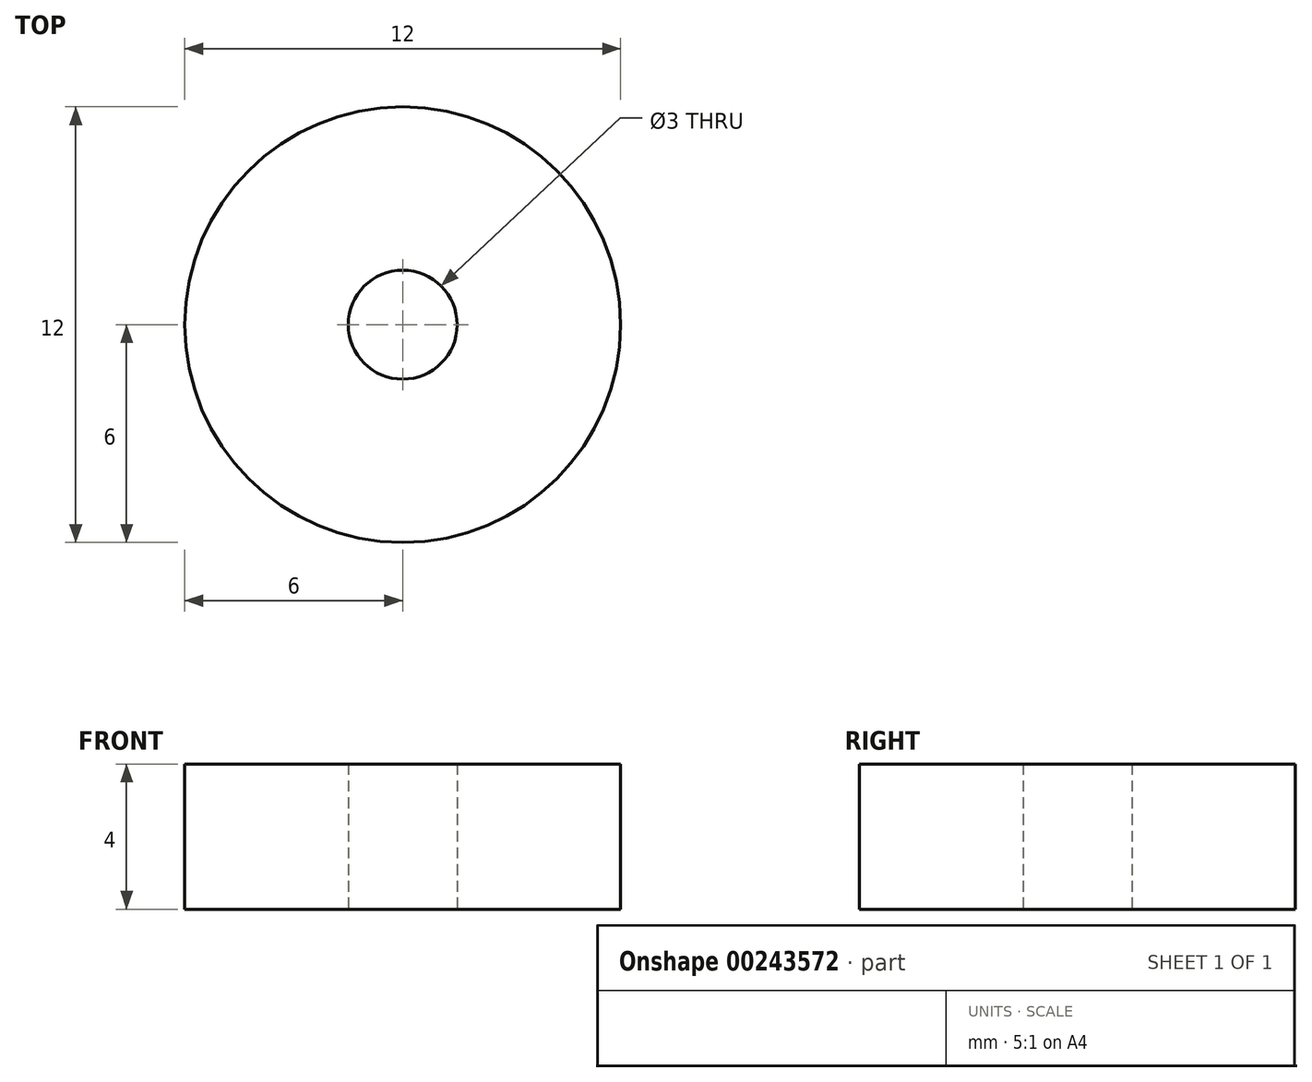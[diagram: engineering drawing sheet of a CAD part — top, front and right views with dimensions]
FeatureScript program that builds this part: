
annotation { "Feature Type Name" : "Feature", "Feature Type Description" : "" }
export const myFeature = defineFeature(function(context is Context, id is Id, definition is map)
    precondition{}
    {
        {
            var Q0;
            Q0=qCreatedBy(makeId("Top.planeOp"),FACE);
            var sketch = newSketch(context, id + "F0", { "sketchPlane" : qUnion([Q0])});
            skCircle(sketch, "E0", {"center": v(0, 0) * mm, "radius": 6 * mm});
            skCircle(sketch, "E1", {"center": v(0, 0) * mm, "radius": 1.5 * mm});
            skSolve(sketch);
        }
        {
            var Q0;
            Q0=makeQuery(id+"F0.imprint","IMPRINT",FACE,{"disambiguationData":[TD([[makeQuery(id+"F0.imprint","IMPRINT",EDGE,{"derivedFrom":sQuery(id+"F0.wireOp",EDGE,"E0")}),1.0]])]});
            extrude(context, id + "F1", {"entities" : qUnion([Q0]), "depth" : 4 * mm});
        }
    });
